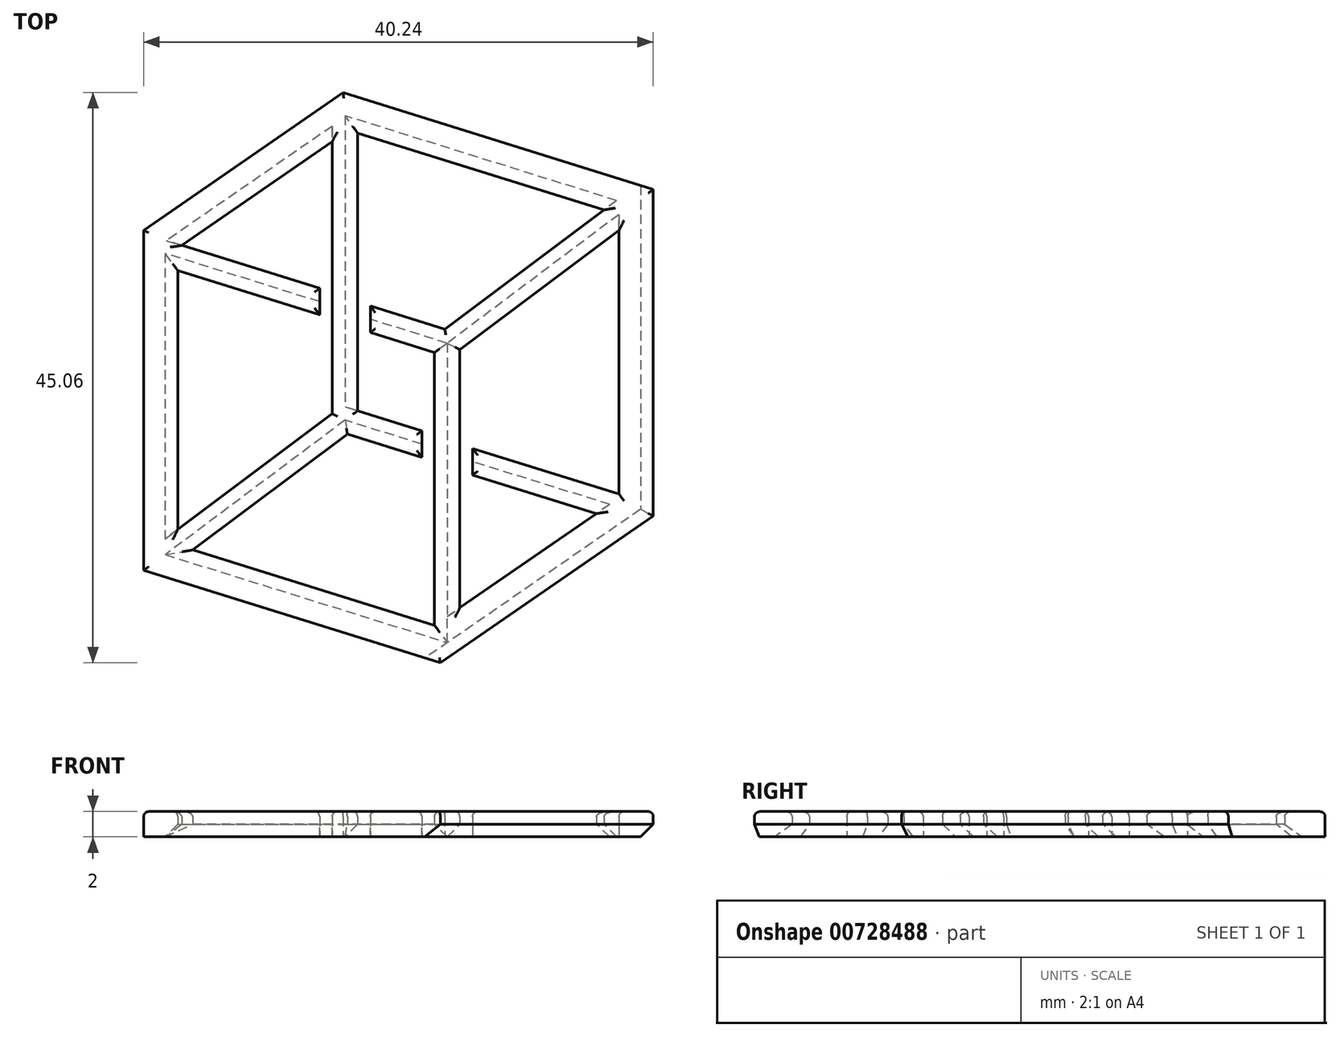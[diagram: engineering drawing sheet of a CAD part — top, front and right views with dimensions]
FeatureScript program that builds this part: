
annotation { "Feature Type Name" : "Feature", "Feature Type Description" : "" }
export const myFeature = defineFeature(function(context is Context, id is Id, definition is map)
    precondition{}
    {
        {
            var Q0;
            Q0=qCreatedBy(makeId("Top.planeOp"),FACE);
            var sketch = newSketch(context, id + "F0", { "sketchPlane" : qUnion([Q0])});
            skLineSegment(sketch, "E0", {"start": v(-29.56, 5.99) * mm, "end": v(-13.82, 16.86) * mm});
            skLineSegment(sketch, "E1", {"start": v(-13.82, 16.86) * mm, "end": v(10.68, 9.2) * mm});
            skLineSegment(sketch, "E2", {"start": v(10.68, 9.2) * mm, "end": v(10.68, -16.6) * mm});
            skLineSegment(sketch, "E3", {"start": v(10.68, -16.6) * mm, "end": v(-6.14, -28.2) * mm});
            skLineSegment(sketch, "E4", {"start": v(-6.14, -28.2) * mm, "end": v(-29.56, -20.9) * mm});
            skLineSegment(sketch, "E5", {"start": v(-29.56, -20.9) * mm, "end": v(-29.56, 5.99) * mm});
            skLineSegment(sketch, "E6.0", {"start": v(-6.59, -25.24) * mm, "end": v(-26.86, -18.9) * mm});
            skLineSegment(sketch, "E6.1", {"start": v(-26.86, 4.57) * mm, "end": v(-13.37, 13.89) * mm});
            skLineSegment(sketch, "E6.2", {"start": v(-13.37, 13.89) * mm, "end": v(7.98, 7.22) * mm});
            skLineSegment(sketch, "E6.3", {"start": v(-26.86, -18.9) * mm, "end": v(-26.86, 4.57) * mm});
            skLineSegment(sketch, "E6.4", {"start": v(7.98, 7.22) * mm, "end": v(7.98, -15.18) * mm});
            skLineSegment(sketch, "E6.5", {"start": v(7.98, -15.18) * mm, "end": v(-6.59, -25.24) * mm});
            skLineSegment(sketch, "E7", {"start": v(-26.86, -18.9) * mm, "end": v(-13.66, -9.02) * mm});
            skLineSegment(sketch, "E8", {"start": v(7.98, 7.22) * mm, "end": v(-5.59, -2.94) * mm});
            skLineSegment(sketch, "E9", {"start": v(-5.59, -2.94) * mm, "end": v(-5.59, -24.55) * mm});
            skLineSegment(sketch, "E10", {"start": v(-13.66, -9.02) * mm, "end": v(-13.66, 13.68) * mm});
            skArc(sketch, "E11.0.startCap", {"start": v(-6.59, -2.94) * mm, "mid": v(-5.59, -1.94) * mm, "end": v(-4.59, -2.94) * mm});
            skLineSegment(sketch, "E11.0.left", {"start": v(-4.59, -2.94) * mm, "end": v(-4.59, -23.85) * mm});
            skLineSegment(sketch, "E11.0.right", {"start": v(-6.59, -2.94) * mm, "end": v(-6.59, -25.24) * mm});
            skArc(sketch, "E11.1.startCap", {"start": v(-5.3, -1.99) * mm, "mid": v(-4.63, -3.24) * mm, "end": v(-5.89, -3.9) * mm});
            skLineSegment(sketch, "E11.1.left", {"start": v(-5.89, -3.9) * mm, "end": v(-11.66, -2.1) * mm});
            skLineSegment(sketch, "E11.1.right", {"start": v(-5.3, -1.99) * mm, "end": v(-11.66, 0) * mm});
            skLineSegment(sketch, "E11.2.left", {"start": v(-26.55, 4.78) * mm, "end": v(-15.66, 1.39) * mm});
            skLineSegment(sketch, "E11.2.right", {"start": v(-26.86, 2.79) * mm, "end": v(-15.66, -0.7) * mm});
            skArc(sketch, "E11.3.endCap", {"start": v(-14.26, -8.22) * mm, "mid": v(-12.86, -8.42) * mm, "end": v(-13.06, -9.82) * mm});
            skLineSegment(sketch, "E11.3.left", {"start": v(-26.86, -17.66) * mm, "end": v(-14.26, -8.22) * mm});
            skLineSegment(sketch, "E11.3.right", {"start": v(-25.69, -19.28) * mm, "end": v(-13.06, -9.82) * mm});
            skArc(sketch, "E11.4.startCap", {"start": v(-12.66, -9.02) * mm, "mid": v(-13.66, -10.02) * mm, "end": v(-14.66, -9.02) * mm});
            skLineSegment(sketch, "E11.4.left", {"start": v(-14.66, -9.02) * mm, "end": v(-14.66, 13) * mm});
            skLineSegment(sketch, "E11.4.right", {"start": v(-12.66, -9.02) * mm, "end": v(-12.66, 13.67) * mm});
            skLineSegment(sketch, "E12", {"start": v(-3.59, -11.98) * mm, "end": v(7.57, -15.46) * mm});
            skLineSegment(sketch, "E13.0.left", {"start": v(-3.59, -11.25) * mm, "end": v(7.98, -14.86) * mm});
            skLineSegment(sketch, "E13.0.right", {"start": v(-3.59, -13.35) * mm, "end": v(6.2, -16.4) * mm});
            skArc(sketch, "E13.1.endCap", {"start": v(-4.99, -3.74) * mm, "mid": v(-6.39, -3.54) * mm, "end": v(-6.19, -2.14) * mm});
            skLineSegment(sketch, "E13.1.left", {"start": v(7.98, 5.97) * mm, "end": v(-4.99, -3.74) * mm});
            skLineSegment(sketch, "E13.1.right", {"start": v(6.8, 7.6) * mm, "end": v(-6.19, -2.14) * mm});
            skLineSegment(sketch, "E14", {"start": v(-3.59, -11.25) * mm, "end": v(-3.59, -11.98) * mm});
            skLineSegment(sketch, "E15", {"start": v(-3.59, -11.98) * mm, "end": v(-3.59, -13.35) * mm});
            skLineSegment(sketch, "E16", {"start": v(-11.66, 0) * mm, "end": v(-11.66, -2.1) * mm});
            skLineSegment(sketch, "E17", {"start": v(-15.66, -0.7) * mm, "end": v(-15.66, 1.39) * mm});
            skArc(sketch, "E18.0.startCap", {"start": v(-13.96, -9.98) * mm, "mid": v(-14.62, -8.72) * mm, "end": v(-13.37, -8.07) * mm});
            skLineSegment(sketch, "E18.0.left", {"start": v(-13.37, -8.07) * mm, "end": v(-7.59, -9.87) * mm});
            skLineSegment(sketch, "E18.0.right", {"start": v(-13.96, -9.98) * mm, "end": v(-7.59, -11.96) * mm});
            skLineSegment(sketch, "E19", {"start": v(-7.59, -9.87) * mm, "end": v(-7.59, -11.96) * mm});
            skSolve(sketch);
        }
        {
            var Q0;
            Q0=makeQuery(id+"F0.imprint","IMPRINT",FACE,{"disambiguationData":[TD([[makeQuery(id+"F0.imprint","IMPRINT",EDGE,{"derivedFrom":sQuery(id+"F0.wireOp",EDGE,"E0")}),-1.0]])]});
            var Q1;
            {var subQ1=sQuery(id+"F0.wireOp",EDGE,"E6.2");var subQ6=sQuery(id+"F0.wireOp",EDGE,"E6.1");var subQ10=makeQuery(id+"F0.imprint","INTERSECT",VERTEX,{"derivedFrom":[subQ6,subQ1]});Q1=makeQuery(id+"F0.imprint","IMPRINT",FACE,{"disambiguationData":[TD([[makeQuery(id+"F0.imprint","IMPRINT",EDGE,{"disambiguationData":[TD([[subQ10,1.0]])],"derivedFrom":subQ6}),-1.0]])]});}
            var Q2;
            {var subQ0=sQuery(id+"F0.wireOp",EDGE,"E11.2.right");Q2=makeQuery(id+"F0.imprint","IMPRINT",FACE,{"disambiguationData":[TD([[makeQuery(id+"F0.imprint","IMPRINT",EDGE,{"derivedFrom":subQ0}),1.0]])]});}
            var Q3;
            {var subQ0=sQuery(id+"F0.wireOp",EDGE,"E9");var subQ1=sQuery(id+"F0.wireOp",EDGE,"E6.5");var subQ2=makeQuery(id+"F0.imprint","INTERSECT",VERTEX,{"derivedFrom":[subQ1,subQ0]});Q3=makeQuery(id+"F0.imprint","IMPRINT",FACE,{"disambiguationData":[TD([[makeQuery(id+"F0.imprint","IMPRINT",EDGE,{"disambiguationData":[TD([[subQ2,1.0]])],"derivedFrom":subQ1}),-1.0]])]});}
            var Q4;
            {var subQ0=sQuery(id+"F0.wireOp",EDGE,"E6.5");var subQ1=makeQuery(id+"F0.imprint","INTERSECT",VERTEX,{"derivedFrom":[subQ0,sQuery(id+"F0.wireOp",EDGE,"E9")]});Q4=makeQuery(id+"F0.imprint","IMPRINT",FACE,{"disambiguationData":[TD([[makeQuery(id+"F0.imprint","IMPRINT",EDGE,{"disambiguationData":[TD([[subQ1,1.0]])],"derivedFrom":subQ0}),1.0]])]});}
            var Q5;
            {var subQ3=sQuery(id+"F0.wireOp",EDGE,"E11.3.left");var subQ5=sQuery(id+"F0.wireOp",EDGE,"E6.3");var subQ6=makeQuery(id+"F0.imprint","INTERSECT",VERTEX,{"derivedFrom":[subQ5,subQ3]});Q5=makeQuery(id+"F0.imprint","IMPRINT",FACE,{"disambiguationData":[TD([[makeQuery(id+"F0.imprint","IMPRINT",EDGE,{"disambiguationData":[TD([[subQ6,-1.0]])],"derivedFrom":subQ3}),-1.0]])]});}
            var Q6;
            {var subQ0=sQuery(id+"F0.wireOp",EDGE,"E11.1.startCap");var subQ1=sQuery(id+"F0.wireOp",EDGE,"E11.0.left");var subQ2=makeQuery(id+"F0.imprint","INTERSECT",VERTEX,{"derivedFrom":[subQ1,subQ0]});Q6=makeQuery(id+"F0.imprint","IMPRINT",FACE,{"disambiguationData":[TD([[makeQuery(id+"F0.imprint","IMPRINT",EDGE,{"disambiguationData":[TD([[subQ2,-1.0]])],"derivedFrom":subQ1}),1.0]])]});}
            var Q7;
            {var subQ4=sQuery(id+"F0.wireOp",EDGE,"E12");Q7=makeQuery(id+"F0.imprint","IMPRINT",FACE,{"disambiguationData":[TD([[makeQuery(id+"F0.imprint","IMPRINT",EDGE,{"derivedFrom":subQ4}),1.0]])]});}
            var Q8;
            {var subQ0=sQuery(id+"F0.wireOp",EDGE,"E12");Q8=makeQuery(id+"F0.imprint","IMPRINT",FACE,{"disambiguationData":[TD([[makeQuery(id+"F0.imprint","IMPRINT",EDGE,{"derivedFrom":subQ0}),-1.0]])]});}
            var Q9;
            {var subQ1=sQuery(id+"F0.wireOp",EDGE,"E13.1.startCap");Q9=makeQuery(id+"F0.imprint","IMPRINT",FACE,{"disambiguationData":[TD([[makeQuery(id+"F0.imprint","IMPRINT",EDGE,{"derivedFrom":subQ1}),-1.0]])]});}
            var Q10;
            {var subQ0=sQuery(id+"F0.wireOp",EDGE,"E11.3.startCap");Q10=makeQuery(id+"F0.imprint","IMPRINT",FACE,{"disambiguationData":[TD([[makeQuery(id+"F0.imprint","IMPRINT",EDGE,{"derivedFrom":subQ0}),-1.0]])]});}
            var Q11;
            {var subQ1=sQuery(id+"F0.wireOp",EDGE,"E11.0.startCap");Q11=makeQuery(id+"F0.imprint","IMPRINT",FACE,{"disambiguationData":[TD([[makeQuery(id+"F0.imprint","IMPRINT",EDGE,{"derivedFrom":subQ1}),-1.0]])]});}
            var Q12;
            {var subQ3=sQuery(id+"F0.wireOp",EDGE,"E6.4");var subQ5=sQuery(id+"F0.wireOp",EDGE,"E6.5");var subQ8=makeQuery(id+"F0.imprint","INTERSECT",VERTEX,{"derivedFrom":[subQ3,subQ5]});Q12=makeQuery(id+"F0.imprint","IMPRINT",FACE,{"disambiguationData":[TD([[makeQuery(id+"F0.imprint","IMPRINT",EDGE,{"disambiguationData":[TD([[subQ8,1.0]])],"derivedFrom":subQ3}),1.0]])]});}
            var Q13;
            {var subQ5=sQuery(id+"F0.wireOp",EDGE,"E6.0");var subQ7=sQuery(id+"F0.wireOp",EDGE,"E11.3.right");var subQ8=makeQuery(id+"F0.imprint","INTERSECT",VERTEX,{"derivedFrom":[subQ5,subQ7]});Q13=makeQuery(id+"F0.imprint","IMPRINT",FACE,{"disambiguationData":[TD([[makeQuery(id+"F0.imprint","IMPRINT",EDGE,{"disambiguationData":[TD([[subQ8,-1.0]])],"derivedFrom":subQ7}),1.0]])]});}
            var Q14;
            {var subQ3=sQuery(id+"F0.wireOp",EDGE,"E13.1.right");var subQ7=sQuery(id+"F0.wireOp",EDGE,"E6.2");var subQ8=makeQuery(id+"F0.imprint","INTERSECT",VERTEX,{"derivedFrom":[subQ7,subQ3]});Q14=makeQuery(id+"F0.imprint","IMPRINT",FACE,{"disambiguationData":[TD([[makeQuery(id+"F0.imprint","IMPRINT",EDGE,{"disambiguationData":[TD([[subQ8,-1.0]])],"derivedFrom":subQ3}),1.0]])]});}
            var Q15;
            {var subQ6=sQuery(id+"F0.wireOp",EDGE,"E11.4.endCap");Q15=makeQuery(id+"F0.imprint","IMPRINT",FACE,{"disambiguationData":[TD([[makeQuery(id+"F0.imprint","IMPRINT",EDGE,{"derivedFrom":subQ6}),-1.0]])]});}
            var Q16;
            {var subQ5=sQuery(id+"F0.wireOp",EDGE,"E6.5");var subQ7=sQuery(id+"F0.wireOp",EDGE,"E9");var subQ8=makeQuery(id+"F0.imprint","INTERSECT",VERTEX,{"derivedFrom":[subQ5,subQ7]});Q16=makeQuery(id+"F0.imprint","IMPRINT",FACE,{"disambiguationData":[TD([[makeQuery(id+"F0.imprint","IMPRINT",EDGE,{"disambiguationData":[TD([[subQ8,-1.0]])],"derivedFrom":subQ5}),-1.0]])]});}
            var Q17;
            {var subQ0=sQuery(id+"F0.wireOp",EDGE,"E16");Q17=makeQuery(id+"F0.imprint","IMPRINT",FACE,{"disambiguationData":[TD([[makeQuery(id+"F0.imprint","IMPRINT",EDGE,{"derivedFrom":subQ0}),1.0]])]});}
            var Q18;
            {var subQ0=sQuery(id+"F0.wireOp",EDGE,"E19");Q18=makeQuery(id+"F0.imprint","IMPRINT",FACE,{"disambiguationData":[TD([[makeQuery(id+"F0.imprint","IMPRINT",EDGE,{"derivedFrom":subQ0}),-1.0]])]});}
            var Q19;
            {var subQ1=sQuery(id+"F0.wireOp",EDGE,"E6.1");var subQ5=sQuery(id+"F0.wireOp",EDGE,"E10");var subQ6=makeQuery(id+"F0.imprint","INTERSECT",VERTEX,{"derivedFrom":[subQ1,subQ5]});Q19=makeQuery(id+"F0.imprint","IMPRINT",FACE,{"disambiguationData":[TD([[makeQuery(id+"F0.imprint","IMPRINT",EDGE,{"disambiguationData":[TD([[subQ6,1.0]])],"derivedFrom":subQ1}),-1.0]])]});}
            var Q20;
            {var subQ0=sQuery(id+"F0.wireOp",EDGE,"E6.3");var subQ1=sQuery(id+"F0.wireOp",EDGE,"E6.1");var subQ2=makeQuery(id+"F0.imprint","INTERSECT",VERTEX,{"derivedFrom":[subQ1,subQ0]});Q20=makeQuery(id+"F0.imprint","IMPRINT",FACE,{"disambiguationData":[TD([[makeQuery(id+"F0.imprint","IMPRINT",EDGE,{"disambiguationData":[TD([[subQ2,-1.0]])],"derivedFrom":subQ1}),1.0]])]});}
            var Q21;
            {var subQ2=sQuery(id+"F0.wireOp",EDGE,"E8");var subQ4=sQuery(id+"F0.wireOp",EDGE,"E9");var subQ5=makeQuery(id+"F0.imprint","INTERSECT",VERTEX,{"derivedFrom":[subQ2,subQ4]});Q21=makeQuery(id+"F0.imprint","IMPRINT",FACE,{"disambiguationData":[TD([[makeQuery(id+"F0.imprint","IMPRINT",EDGE,{"disambiguationData":[TD([[subQ5,1.0]])],"derivedFrom":subQ2}),1.0]])]});}
            var Q22;
            {var subQ0=sQuery(id+"F0.wireOp",EDGE,"E13.1.endCap");var subQ1=sQuery(id+"F0.wireOp",EDGE,"E11.0.right");var subQ2=makeQuery(id+"F0.imprint","INTERSECT",VERTEX,{"derivedFrom":[subQ1,subQ0]});Q22=makeQuery(id+"F0.imprint","IMPRINT",FACE,{"disambiguationData":[TD([[makeQuery(id+"F0.imprint","IMPRINT",EDGE,{"disambiguationData":[TD([[subQ2,-1.0]])],"derivedFrom":subQ1}),1.0]])]});}
            var Q23;
            {var subQ3=sQuery(id+"F0.wireOp",EDGE,"E7");var subQ5=sQuery(id+"F0.wireOp",EDGE,"E10");var subQ6=makeQuery(id+"F0.imprint","INTERSECT",VERTEX,{"derivedFrom":[subQ3,subQ5]});Q23=makeQuery(id+"F0.imprint","IMPRINT",FACE,{"disambiguationData":[TD([[makeQuery(id+"F0.imprint","IMPRINT",EDGE,{"disambiguationData":[TD([[subQ6,1.0]])],"derivedFrom":subQ3}),1.0]])]});}
            var Q24;
            {var subQ0=sQuery(id+"F0.wireOp",EDGE,"E11.3.endCap");Q24=makeQuery(id+"F0.imprint","IMPRINT",FACE,{"disambiguationData":[TD([[makeQuery(id+"F0.imprint","IMPRINT",EDGE,{"derivedFrom":subQ0}),-1.0]])]});}
            var Q25;
            {var subQ0=sQuery(id+"F0.wireOp",EDGE,"E11.3.endCap");Q25=makeQuery(id+"F0.imprint","IMPRINT",FACE,{"disambiguationData":[TD([[makeQuery(id+"F0.imprint","IMPRINT",EDGE,{"derivedFrom":subQ0}),1.0]])]});}
            var Q26;
            {var subQ0=sQuery(id+"F0.wireOp",EDGE,"E11.4.startCap");var subQ1=sQuery(id+"F0.wireOp",EDGE,"E11.3.right");var subQ2=makeQuery(id+"F0.imprint","INTERSECT",VERTEX,{"derivedFrom":[subQ1,subQ0]});Q26=makeQuery(id+"F0.imprint","IMPRINT",FACE,{"disambiguationData":[TD([[makeQuery(id+"F0.imprint","IMPRINT",EDGE,{"disambiguationData":[TD([[subQ2,1.0]])],"derivedFrom":subQ1}),1.0]])]});}
            var Q27;
            {var subQ0=sQuery(id+"F0.wireOp",EDGE,"E11.1.startCap");var subQ1=sQuery(id+"F0.wireOp",EDGE,"E11.0.left");var subQ2=makeQuery(id+"F0.imprint","INTERSECT",VERTEX,{"derivedFrom":[subQ1,subQ0]});Q27=makeQuery(id+"F0.imprint","IMPRINT",FACE,{"disambiguationData":[TD([[makeQuery(id+"F0.imprint","IMPRINT",EDGE,{"disambiguationData":[TD([[subQ2,-1.0]])],"derivedFrom":subQ1}),-1.0]])]});}
            var Q28;
            {var subQ0=sQuery(id+"F0.wireOp",EDGE,"E11.0.startCap");Q28=makeQuery(id+"F0.imprint","IMPRINT",FACE,{"disambiguationData":[TD([[makeQuery(id+"F0.imprint","IMPRINT",EDGE,{"derivedFrom":subQ0}),1.0]])]});}
            var Q29;
            {var subQ0=sQuery(id+"F0.wireOp",EDGE,"E18.0.startCap");var subQ1=sQuery(id+"F0.wireOp",EDGE,"E11.3.left");var subQ2=makeQuery(id+"F0.imprint","INTERSECT",VERTEX,{"derivedFrom":[subQ1,subQ0]});Q29=makeQuery(id+"F0.imprint","IMPRINT",FACE,{"disambiguationData":[TD([[makeQuery(id+"F0.imprint","IMPRINT",EDGE,{"disambiguationData":[TD([[subQ2,1.0]])],"derivedFrom":subQ1}),-1.0]])]});}
            extrude(context, id + "F1", {"entities" : qUnion([Q0, Q1, Q2, Q3, Q4, Q5, Q6, Q7, Q8, Q9, Q10, Q11, Q12, Q13, Q14, Q15, Q16, Q17, Q18, Q19, Q20, Q21, Q22, Q23, Q24, Q25, Q26, Q27, Q28, Q29]), "depth" : 2 * mm, "offsetDistance" : 25 * mm});
        }
        {
            var Q0;
            Q0=makeQuery(id+"F1.opExtrude","CAP_EDGE",EDGE,{"disambiguationData":[OSD([sQuery(id+"F0.wireOp",EDGE,"E11.0.right")])],"isStart":true});
            var Q1;
            Q1=makeQuery(id+"F1.opExtrude","CAP_EDGE",EDGE,{"disambiguationData":[OSD([sQuery(id+"F0.wireOp",EDGE,"E11.4.right")])],"isStart":true});
            var Q2;
            Q2=makeQuery(id+"F1.opExtrude","CAP_EDGE",EDGE,{"disambiguationData":[OSD([sQuery(id+"F0.wireOp",EDGE,"E6.1")])],"isStart":true});
            var Q3;
            Q3=makeQuery(id+"F1.opExtrude","CAP_EDGE",EDGE,{"disambiguationData":[OSD([sQuery(id+"F0.wireOp",EDGE,"E6.3")])],"isStart":true});
            var Q4;
            Q4=makeQuery(id+"F1.opExtrude","CAP_EDGE",EDGE,{"disambiguationData":[OSD([sQuery(id+"F0.wireOp",EDGE,"E11.2.right")])],"isStart":true});
            var Q5;
            Q5=makeQuery(id+"F1.opExtrude","CAP_EDGE",EDGE,{"disambiguationData":[OSD([sQuery(id+"F0.wireOp",EDGE,"E11.3.right")])],"isStart":true});
            var Q6;
            Q6=makeQuery(id+"F1.opExtrude","CAP_EDGE",EDGE,{"disambiguationData":[OSD([sQuery(id+"F0.wireOp",EDGE,"E13.0.right")])],"isStart":true});
            var Q7;
            Q7=makeQuery(id+"F1.opExtrude","CAP_EDGE",EDGE,{"disambiguationData":[OSD([sQuery(id+"F0.wireOp",EDGE,"E18.0.right")])],"isStart":true});
            var Q8;
            Q8=makeQuery(id+"F1.opExtrude","CAP_EDGE",EDGE,{"disambiguationData":[OSD([sQuery(id+"F0.wireOp",EDGE,"E11.1.left")])],"isStart":true});
            var Q9;
            Q9=makeQuery(id+"F1.opExtrude","CAP_EDGE",EDGE,{"disambiguationData":[OSD([sQuery(id+"F0.wireOp",EDGE,"E11.0.left")])],"isStart":true});
            var Q10;
            Q10=makeQuery(id+"F1.opExtrude","CAP_EDGE",EDGE,{"disambiguationData":[OSD([sQuery(id+"F0.wireOp",EDGE,"E13.1.left")])],"isStart":true});
            var Q11;
            Q11=makeQuery(id+"F1.opExtrude","CAP_EDGE",EDGE,{"disambiguationData":[OSD([sQuery(id+"F0.wireOp",EDGE,"E2")])],"isStart":true});
            var Q12;
            Q12=makeQuery(id+"F1.opExtrude","CAP_EDGE",EDGE,{"disambiguationData":[OSD([sQuery(id+"F0.wireOp",EDGE,"E6.2")])],"isStart":true});
            var Q13;
            Q13=makeQuery(id+"F1.opExtrude","CAP_EDGE",EDGE,{"disambiguationData":[OSD([sQuery(id+"F0.wireOp",EDGE,"E3")])],"isStart":true});
            var Q14;
            Q14=makeQuery(id+"F1.opExtrude","CAP_EDGE",EDGE,{"disambiguationData":[OSD([sQuery(id+"F0.wireOp",EDGE,"E6.0")])],"isStart":true});
            chamfer(context, id + "F2", {"entities" : qUnion([Q0, Q1, Q2, Q3, Q4, Q5, Q6, Q7, Q8, Q9, Q10, Q11, Q12, Q13, Q14]), "width" : 1 * mm});
        }
        {
            var Q0;
            Q0=makeQuery(id+"F1.opExtrude","CAP_EDGE",EDGE,{"disambiguationData":[OSD([sQuery(id+"F0.wireOp",EDGE,"E4")])],"isStart":false});
            var Q1;
            Q1=makeQuery(id+"F1.opExtrude","CAP_EDGE",EDGE,{"disambiguationData":[OSD([sQuery(id+"F0.wireOp",EDGE,"E3")])],"isStart":false});
            var Q2;
            Q2=makeQuery(id+"F1.opExtrude","CAP_EDGE",EDGE,{"disambiguationData":[OSD([sQuery(id+"F0.wireOp",EDGE,"E2")])],"isStart":false});
            var Q3;
            Q3=makeQuery(id+"F1.opExtrude","CAP_EDGE",EDGE,{"disambiguationData":[OSD([sQuery(id+"F0.wireOp",EDGE,"E1")])],"isStart":false});
            var Q4;
            Q4=makeQuery(id+"F1.opExtrude","CAP_EDGE",EDGE,{"disambiguationData":[OSD([sQuery(id+"F0.wireOp",EDGE,"E0")])],"isStart":false});
            var Q5;
            Q5=makeQuery(id+"F1.opExtrude","CAP_EDGE",EDGE,{"disambiguationData":[OSD([sQuery(id+"F0.wireOp",EDGE,"E5")])],"isStart":false});
            var Q6;
            Q6=makeQuery(id+"F1.opExtrude","CAP_EDGE",EDGE,{"disambiguationData":[OSD([sQuery(id+"F0.wireOp",EDGE,"E6.4")])],"isStart":false});
            var Q7;
            Q7=makeQuery(id+"F1.opExtrude","CAP_EDGE",EDGE,{"disambiguationData":[OSD([sQuery(id+"F0.wireOp",EDGE,"E6.5")])],"isStart":false});
            var Q8;
            Q8=makeQuery(id+"F1.opExtrude","CAP_EDGE",EDGE,{"disambiguationData":[OSD([sQuery(id+"F0.wireOp",EDGE,"E6.0")])],"isStart":false});
            var Q9;
            Q9=makeQuery(id+"F1.opExtrude","CAP_EDGE",EDGE,{"disambiguationData":[OSD([sQuery(id+"F0.wireOp",EDGE,"E6.3")])],"isStart":false});
            var Q10;
            Q10=makeQuery(id+"F1.opExtrude","CAP_EDGE",EDGE,{"disambiguationData":[OSD([sQuery(id+"F0.wireOp",EDGE,"E11.2.right")])],"isStart":false});
            var Q11;
            Q11=makeQuery(id+"F1.opExtrude","CAP_EDGE",EDGE,{"disambiguationData":[OSD([sQuery(id+"F0.wireOp",EDGE,"E11.2.left")])],"isStart":false});
            var Q12;
            Q12=makeQuery(id+"F1.opExtrude","CAP_EDGE",EDGE,{"disambiguationData":[OSD([sQuery(id+"F0.wireOp",EDGE,"E11.4.left")])],"isStart":false});
            var Q13;
            Q13=makeQuery(id+"F1.opExtrude","CAP_EDGE",EDGE,{"disambiguationData":[OSD([sQuery(id+"F0.wireOp",EDGE,"E11.4.right")])],"isStart":false});
            var Q14;
            Q14=makeQuery(id+"F1.opExtrude","CAP_EDGE",EDGE,{"disambiguationData":[OSD([sQuery(id+"F0.wireOp",EDGE,"E13.1.left")])],"isStart":false});
            var Q15;
            Q15=makeQuery(id+"F1.opExtrude","CAP_EDGE",EDGE,{"disambiguationData":[OSD([sQuery(id+"F0.wireOp",EDGE,"E13.1.right")])],"isStart":false});
            var Q16;
            Q16=makeQuery(id+"F1.opExtrude","CAP_FACE",FACE,{"disambiguationData":[OSD([sQuery(id+"F0.wireOp",EDGE,"E0"),sQuery(id+"F0.wireOp",EDGE,"E1"),sQuery(id+"F0.wireOp",EDGE,"E2"),sQuery(id+"F0.wireOp",EDGE,"E3"),sQuery(id+"F0.wireOp",EDGE,"E4"),sQuery(id+"F0.wireOp",EDGE,"E5"),sQuery(id+"F0.wireOp",EDGE,"E6.0"),sQuery(id+"F0.wireOp",EDGE,"E6.1"),sQuery(id+"F0.wireOp",EDGE,"E6.2"),sQuery(id+"F0.wireOp",EDGE,"E6.3"),sQuery(id+"F0.wireOp",EDGE,"E6.4"),sQuery(id+"F0.wireOp",EDGE,"E6.5"),sQuery(id+"F0.wireOp",EDGE,"E11.0.left"),sQuery(id+"F0.wireOp",EDGE,"E11.0.right"),sQuery(id+"F0.wireOp",EDGE,"E11.1.left"),sQuery(id+"F0.wireOp",EDGE,"E11.1.right"),sQuery(id+"F0.wireOp",EDGE,"E11.2.left"),sQuery(id+"F0.wireOp",EDGE,"E11.2.right"),sQuery(id+"F0.wireOp",EDGE,"E11.3.left"),sQuery(id+"F0.wireOp",EDGE,"E11.3.right"),sQuery(id+"F0.wireOp",EDGE,"E11.4.left"),sQuery(id+"F0.wireOp",EDGE,"E11.4.right"),sQuery(id+"F0.wireOp",EDGE,"E13.0.left"),sQuery(id+"F0.wireOp",EDGE,"E13.0.right"),sQuery(id+"F0.wireOp",EDGE,"E13.1.left"),sQuery(id+"F0.wireOp",EDGE,"E13.1.right"),sQuery(id+"F0.wireOp",EDGE,"E14"),sQuery(id+"F0.wireOp",EDGE,"E15"),sQuery(id+"F0.wireOp",EDGE,"E16"),sQuery(id+"F0.wireOp",EDGE,"E17"),sQuery(id+"F0.wireOp",EDGE,"E18.0.left"),sQuery(id+"F0.wireOp",EDGE,"E18.0.right"),sQuery(id+"F0.wireOp",EDGE,"E19")])],"isStart":false});
            fillet(context, id + "F3", {"entities" : qUnion([Q0, Q1, Q2, Q3, Q4, Q5, Q6, Q7, Q8, Q9, Q10, Q11, Q12, Q13, Q14, Q15, Q16]), "radius" : .4 * mm, "tangentPropagation" : true, "allowEdgeOverflow" : false});
        }
    });
